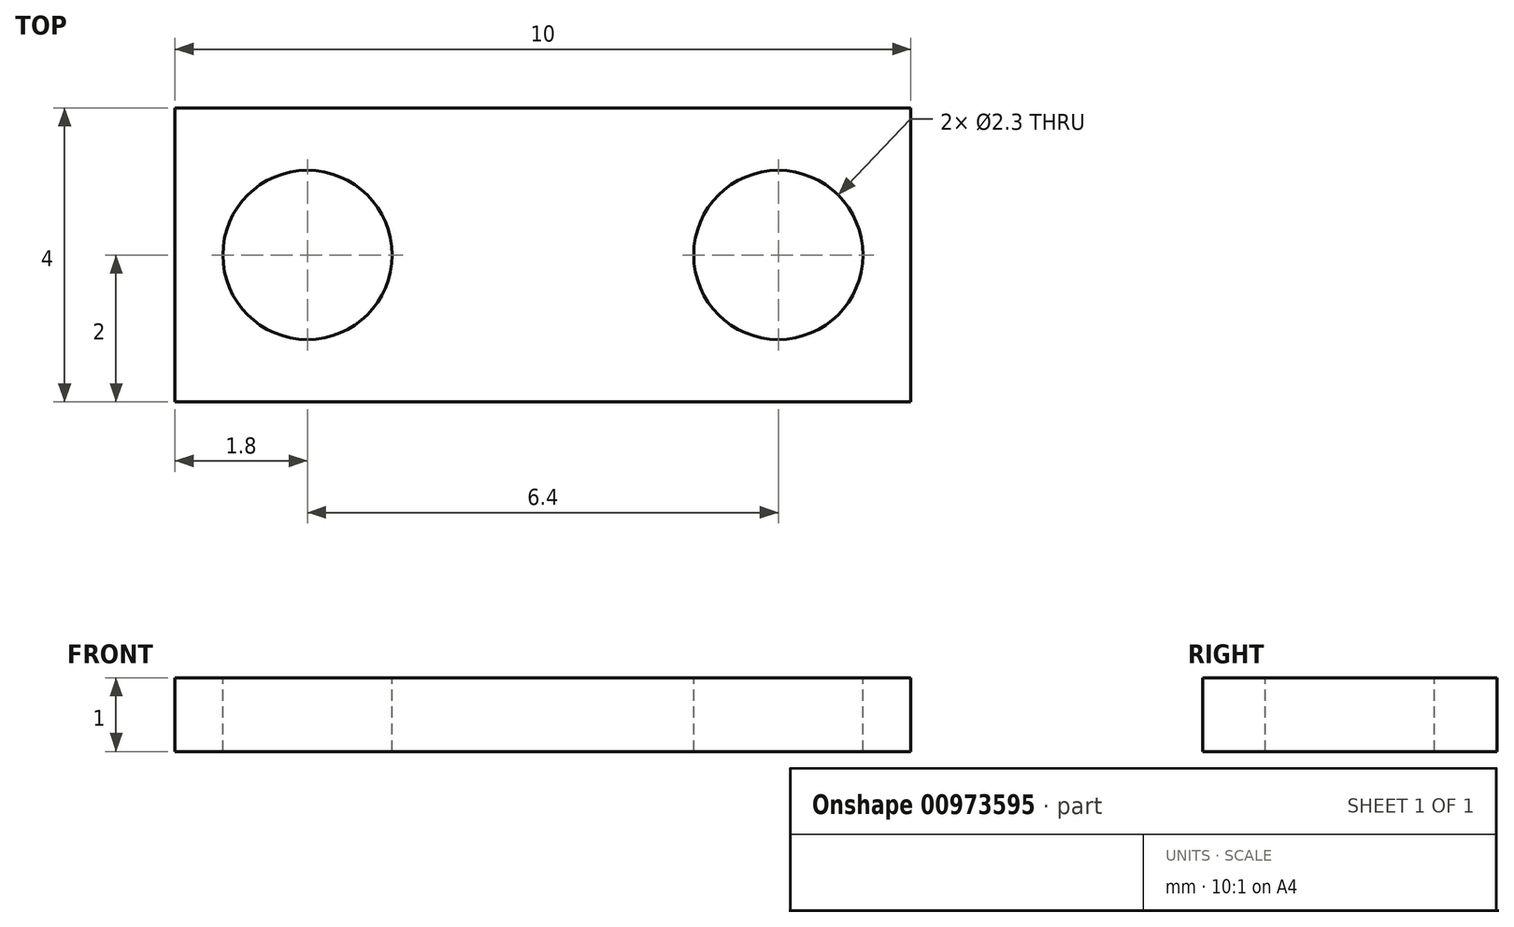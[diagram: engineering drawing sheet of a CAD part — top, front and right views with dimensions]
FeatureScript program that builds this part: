
annotation { "Feature Type Name" : "Feature", "Feature Type Description" : "" }
export const myFeature = defineFeature(function(context is Context, id is Id, definition is map)
    precondition{}
    {
        {
            var Q0;
            Q0=qCreatedBy(makeId("Top.planeOp"),FACE);
            var sketch = newSketch(context, id + "F0", { "sketchPlane" : qUnion([Q0])});
            skLineSegment(sketch, "E0.top", {"start": v(-5, -2) * mm, "end": v(5, -2) * mm});
            skLineSegment(sketch, "E0.left", {"start": v(-5, 2) * mm, "end": v(-5, -2) * mm});
            skLineSegment(sketch, "E0.right", {"start": v(5, 2) * mm, "end": v(5, -2) * mm});
            skLineSegment(sketch, "E1", {"start": v(-8.08, 0) * mm, "end": v(8.08, 0) * mm, "construction": true});
            skLineSegment(sketch, "E2", {"start": v(0, 4.1) * mm, "end": v(0, -4.67) * mm, "construction": true});
            skLineSegment(sketch, "E3", {"start": v(-5, 2) * mm, "end": v(5, 2) * mm});
            skSolve(sketch);
        }
        {
            var Q0;
            Q0 = qSketchRegion(id + "F0", true);
            extrude(context, id + "F1", {"entities" : qUnion([Q0]), "depth" : 1 * mm, "offsetDistance" : 25 * mm});
        }
        {
            var Q0;
            Q0=makeQuery(id+"F1.opExtrude","CAP_FACE",FACE,{"disambiguationData":[OSD([sQuery(id+"F0.wireOp",EDGE,"E0.top"),sQuery(id+"F0.wireOp",EDGE,"E0.left"),sQuery(id+"F0.wireOp",EDGE,"E0.right"),sQuery(id+"F0.wireOp",EDGE,"E3")])],"isStart":false});
            var sketch = newSketch(context, id + "F2", { "sketchPlane" : qUnion([Q0])});
            skPoint(sketch, "E4", {"position": v(-3.2, 0) * mm});
            skPoint(sketch, "E5", {"position": v(3.2, 0) * mm});
            skLineSegment(sketch, "E6", {"start": v(-5.62, 0) * mm, "end": v(5.7, 0) * mm, "construction": true});
            skPoint(sketch, "E6.endSnap0", {"position": v(5, 0) * mm});
            skLineSegment(sketch, "E7", {"start": v(0, 2.43) * mm, "end": v(0, -2.95) * mm, "construction": true});
            skSolve(sketch);
        }
        {
            var Q0;
            Q0=sQuery(id+"F2.wireOp",VERTEX,"E4");
            var Q1;
            Q1=sQuery(id+"F2.wireOp",VERTEX,"E5");
            var Q2;
            Q2=makeQuery(id+"F1.opExtrude","SWEPT_BODY",BODY,{"disambiguationData":[OSD([sQuery(id+"F0.wireOp",EDGE,"E0.top"),sQuery(id+"F0.wireOp",EDGE,"E0.left"),sQuery(id+"F0.wireOp",EDGE,"E0.right"),sQuery(id+"F0.wireOp",EDGE,"E3")])]});
            hole(context, id + "F3", {"style" : HoleStyle.SIMPLE, "endStyle" : HoleEndStyle.THROUGH, "holeDiameter" : 2.3 * mm, "majorDiameter" : 5 * mm, "isTappedThrough" : true, "tappedDepth" : 12 * mm, "tapClearance" : 3, "locations" : qUnion([Q0, Q1]), "scope" : qUnion([Q2])});
        }
    });
